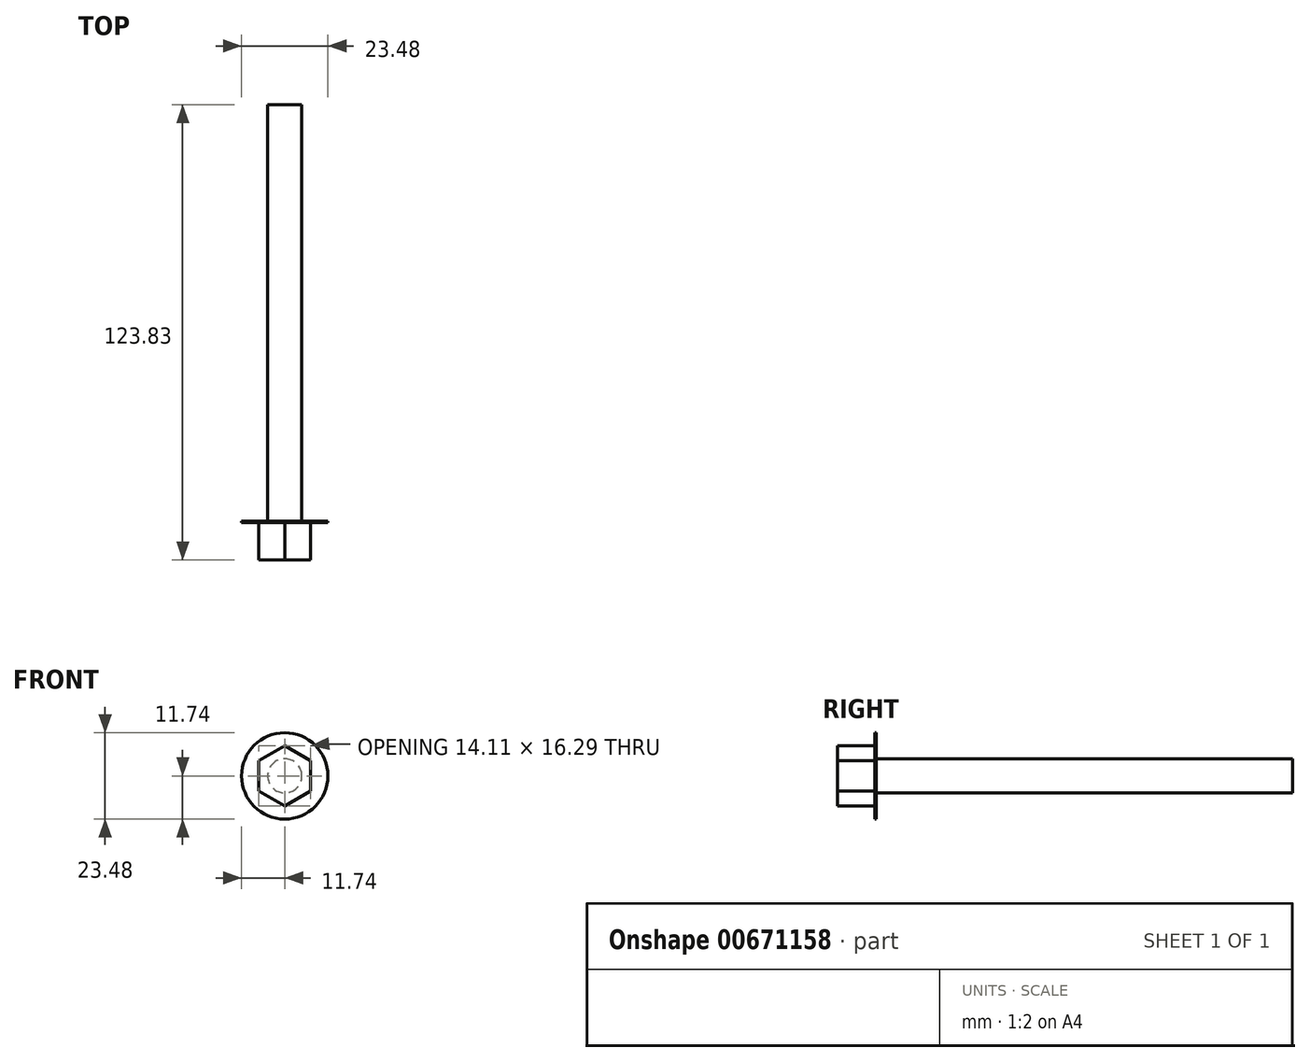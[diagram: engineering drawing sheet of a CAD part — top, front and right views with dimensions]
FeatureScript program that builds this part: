
annotation { "Feature Type Name" : "Feature", "Feature Type Description" : "" }
export const myFeature = defineFeature(function(context is Context, id is Id, definition is map)
    precondition{}
    {
        {
            var Q0;
            Q0=qCreatedBy(makeId("Front.planeOp"),FACE);
            var sketch = newSketch(context, id + "F0", { "sketchPlane" : qUnion([Q0])});
            skCircle(sketch, "E0.cCircle", {"center": v(0, 0) * mm, "radius": 7.05 * mm, "construction": true});
            skLineSegment(sketch, "E0.0", {"start": v(7.05, 4.07) * mm, "end": v(7.05, -4.07) * mm});
            skLineSegment(sketch, "E0.1", {"start": v(7.05, -4.07) * mm, "end": v(0, -8.15) * mm});
            skLineSegment(sketch, "E0.2", {"start": v(0, -8.15) * mm, "end": v(-7.05, -4.07) * mm});
            skLineSegment(sketch, "E0.3", {"start": v(-7.05, -4.07) * mm, "end": v(-7.05, 4.07) * mm});
            skLineSegment(sketch, "E0.4", {"start": v(-7.05, 4.07) * mm, "end": v(0, 8.15) * mm});
            skLineSegment(sketch, "E0.5", {"start": v(0, 8.15) * mm, "end": v(7.05, 4.07) * mm});
            skPoint(sketch, "E0.0.midPoint", {"position": v(7.05, 0) * mm});
            skSolve(sketch);
        }
        {
            var Q0;
            Q0=makeQuery(id+"F0.imprint","IMPRINT",FACE,{"disambiguationData":[TD([[makeQuery(id+"F0.imprint","IMPRINT",EDGE,{"derivedFrom":sQuery(id+"F0.wireOp",EDGE,"E0.0")}),-1.0]])]});
            extrude(context, id + "F1", {"entities" : qUnion([Q0]), "oppositeDirection" : true, "depth" : 10.16 * mm, "offsetDistance" : 25.4 * mm});
        }
        {
            var Q0;
            Q0=makeQuery(id+"F1.opExtrude","CAP_FACE",FACE,{"disambiguationData":[OSD([sQuery(id+"F0.wireOp",EDGE,"E0.0"),sQuery(id+"F0.wireOp",EDGE,"E0.1"),sQuery(id+"F0.wireOp",EDGE,"E0.2"),sQuery(id+"F0.wireOp",EDGE,"E0.3"),sQuery(id+"F0.wireOp",EDGE,"E0.4"),sQuery(id+"F0.wireOp",EDGE,"E0.5")])],"isStart":false});
            var sketch = newSketch(context, id + "F2", { "sketchPlane" : qUnion([Q0])});
            skCircle(sketch, "E1", {"center": v(0, 0) * mm, "radius": 4.64 * mm});
            skSolve(sketch);
        }
        {
            var Q0;
            Q0=makeQuery(id+"F1.opExtrude","CAP_FACE",FACE,{"disambiguationData":[OSD([sQuery(id+"F0.wireOp",EDGE,"E0.0"),sQuery(id+"F0.wireOp",EDGE,"E0.1"),sQuery(id+"F0.wireOp",EDGE,"E0.2"),sQuery(id+"F0.wireOp",EDGE,"E0.3"),sQuery(id+"F0.wireOp",EDGE,"E0.4"),sQuery(id+"F0.wireOp",EDGE,"E0.5")])],"isStart":false});
            var sketch = newSketch(context, id + "F3", { "sketchPlane" : qUnion([Q0])});
            skCircle(sketch, "E2", {"center": v(0, 0) * mm, "radius": 11.74 * mm});
            skCircle(sketch, "E3", {"center": v(0, 0) * mm, "radius": 5.72 * mm});
            skSolve(sketch);
        }
        {
            var Q0;
            Q0=makeQuery(id+"F3.imprint","IMPRINT",FACE,{"disambiguationData":[TD([[makeQuery(id+"F3.imprint","IMPRINT",EDGE,{"derivedFrom":sQuery(id+"F3.wireOp",EDGE,"E2")}),1.0]])]});
            extrude(context, id + "F4", {"entities" : qUnion([Q0]), "depth" : 0.38 * mm, "offsetDistance" : 25.4 * mm});
        }
        {
            var Q0;
            Q0=makeQuery(id+"F2.imprint","IMPRINT",FACE,{"disambiguationData":[TD([[makeQuery(id+"F2.imprint","IMPRINT",EDGE,{"derivedFrom":sQuery(id+"F2.wireOp",EDGE,"E1")}),1.0]])]});
            extrude(context, id + "F5", {"entities" : qUnion([Q0]), "operationType" : NewBodyOperationType.ADD, "depth" : 113.66 * mm, "offsetDistance" : 25.4 * mm});
        }
    });
